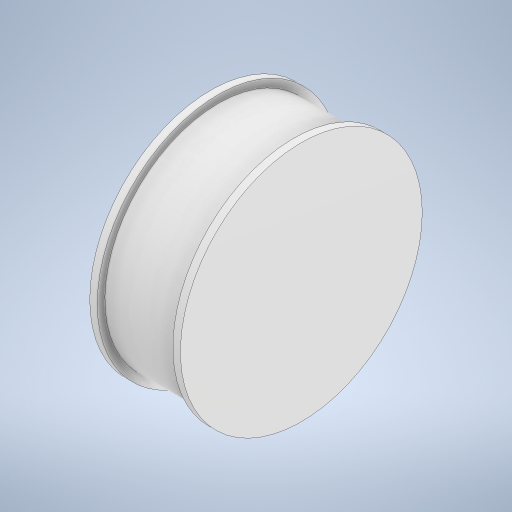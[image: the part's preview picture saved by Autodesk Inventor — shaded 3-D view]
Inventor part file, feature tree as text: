
AUTODESK INVENTOR PART (.ipt)
format: ipt  version: 2023 (Build 270158000, 158)  size: 240,128 bytes
history: native  units: mm
features: extrude x3, sketch x3, other x1
ambient origin geometry x8: Origin, YZ Plane, XZ Plane, XY Plane, X Axis, Y Axis, Z Axis, Center Point
bodies: Body1 (feature_tree)
feature tree (7):
  other  "ソリッド1"
  extrude  "押し出し1"  Depth=30.0mm
  extrude  "押し出し2"  Depth=10.0mm TaperAngle=0.0deg
  extrude  "押し出し3"  Depth=32.0mm
  sketch  "スケッチ1"
  sketch  "スケッチ2"
  sketch  "スケッチ3"
